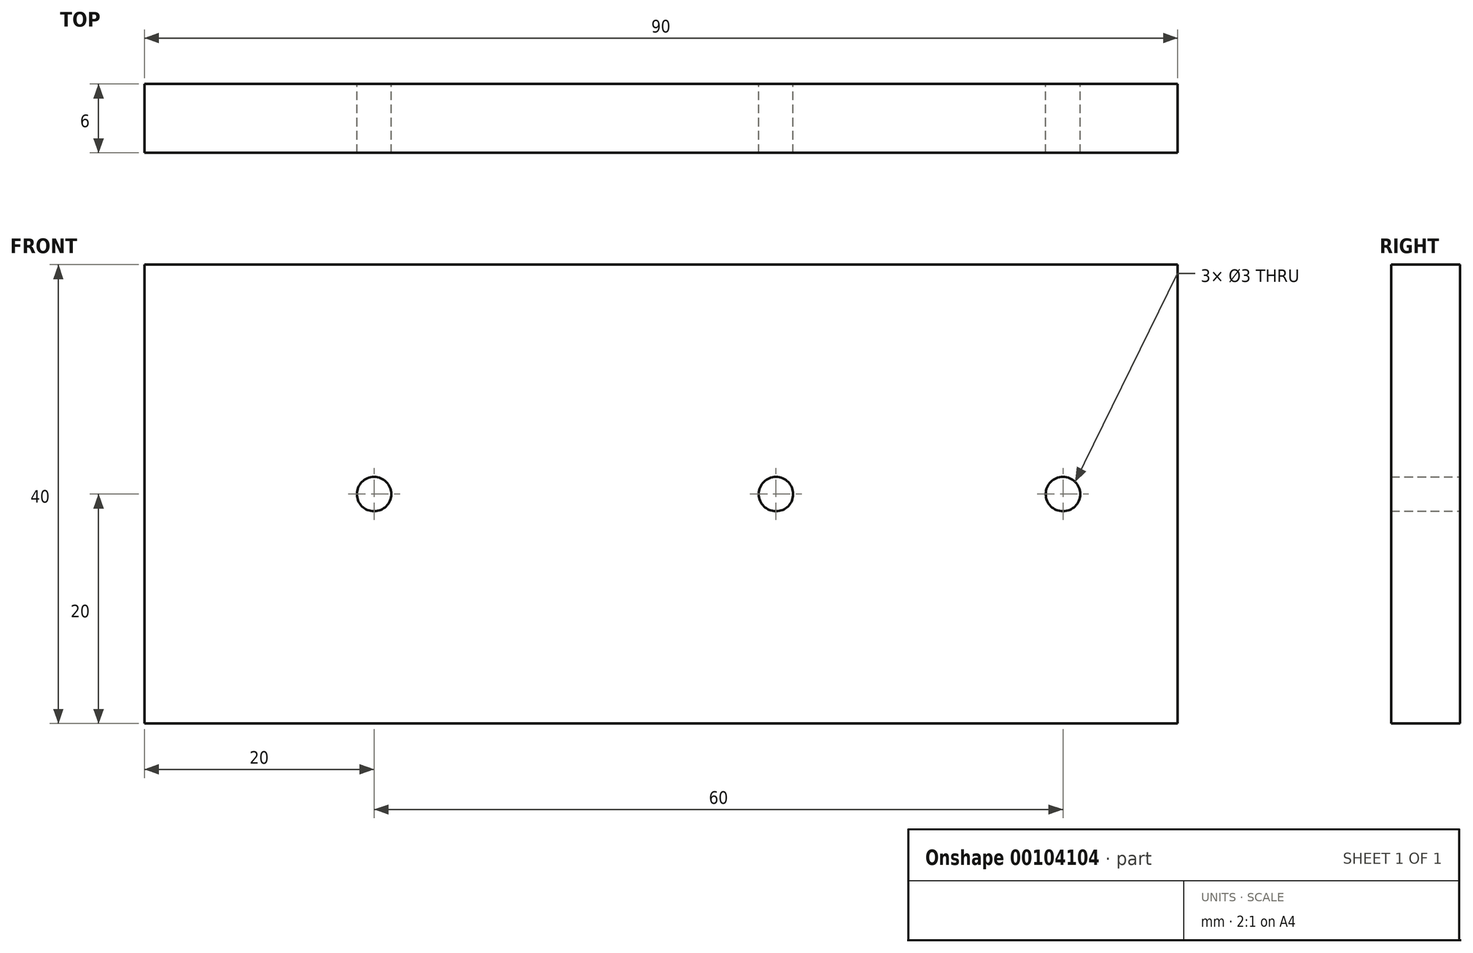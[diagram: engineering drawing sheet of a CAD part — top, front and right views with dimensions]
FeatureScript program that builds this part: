
annotation { "Feature Type Name" : "Feature", "Feature Type Description" : "" }
export const myFeature = defineFeature(function(context is Context, id is Id, definition is map)
    precondition{}
    {
        {
            var Q0;
            Q0=qCreatedBy(makeId("Front.planeOp"),FACE);
            var sketch = newSketch(context, id + "F0", { "sketchPlane" : qUnion([Q0])});
            skLineSegment(sketch, "E0.bottom", {"start": v(0, 0) * mm, "end": v(-90, 0) * mm});
            skLineSegment(sketch, "E0.top", {"start": v(0, 40) * mm, "end": v(-90, 40) * mm});
            skLineSegment(sketch, "E0.left", {"start": v(0, 0) * mm, "end": v(0, 40) * mm});
            skLineSegment(sketch, "E0.right", {"start": v(-90, 0) * mm, "end": v(-90, 40) * mm});
            skPoint(sketch, "E1", {"position": v(-90, 20) * mm});
            skPoint(sketch, "E2", {"position": v(-70, 20) * mm});
            skCircle(sketch, "E3", {"center": v(-70, 20) * mm, "radius": 1.5 * mm});
            skPoint(sketch, "E4", {"position": v(-35, 20) * mm});
            skCircle(sketch, "E5", {"center": v(-35, 20) * mm, "radius": 1.5 * mm});
            skCircle(sketch, "E6", {"center": v(-10, 20) * mm, "radius": 1.5 * mm});
            skPoint(sketch, "E7", {"position": v(0, 20) * mm});
            skSolve(sketch);
        }
        {
            var Q0;
            Q0=qSketchRegion(id+"F0",true);
            extrude(context, id + "F1", {"entities" : qUnion([Q0]), "endBound" : BoundingType.SYMMETRIC, "depth" : 6 * mm});
        }
    });
